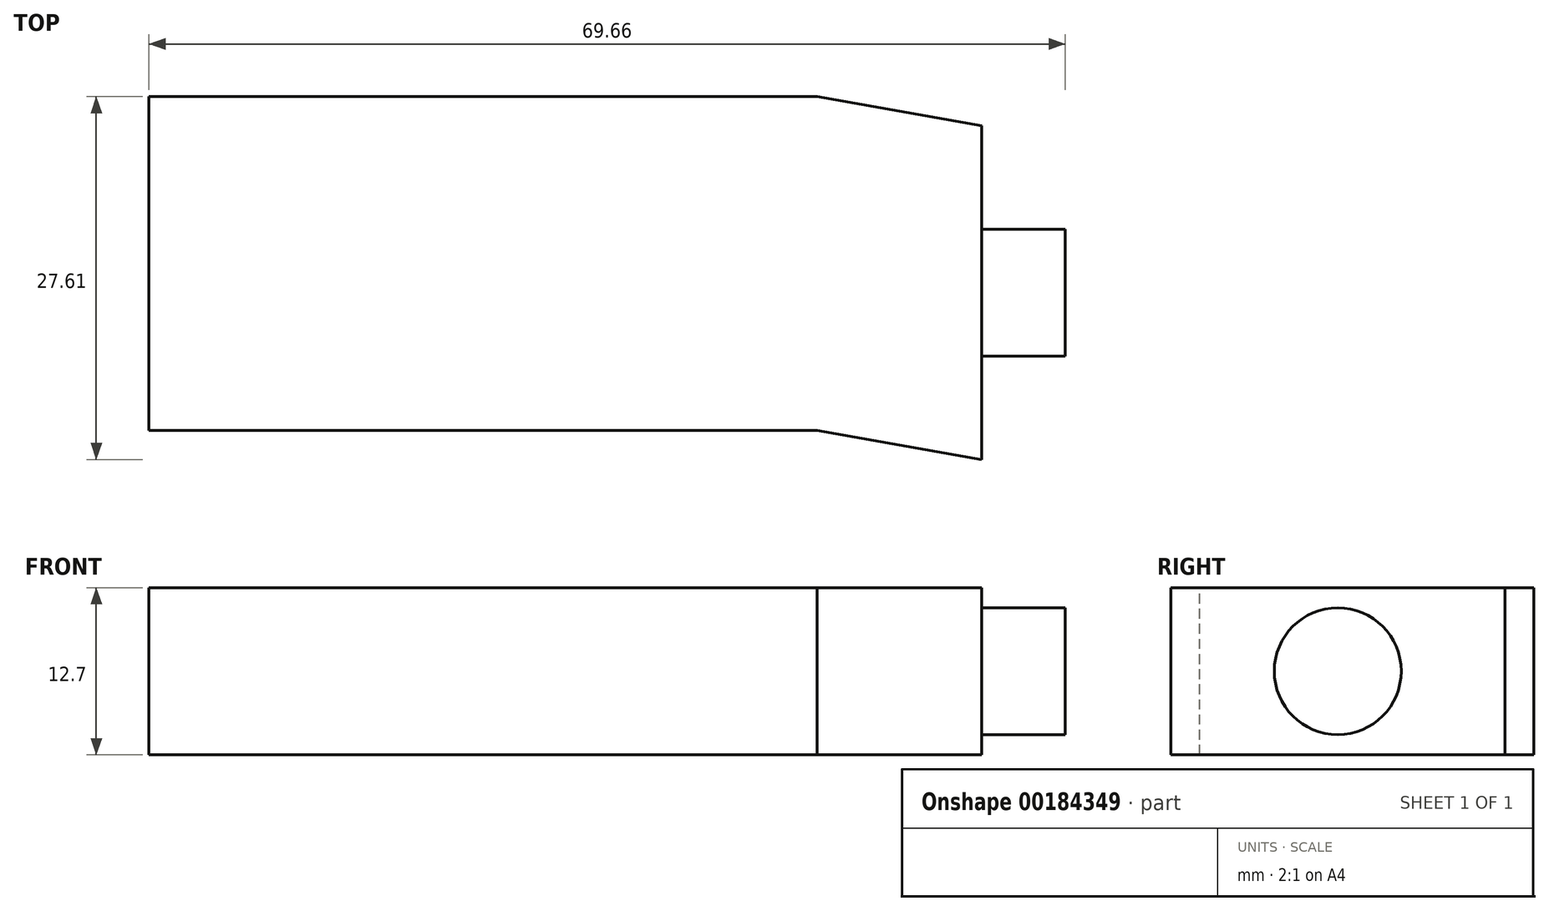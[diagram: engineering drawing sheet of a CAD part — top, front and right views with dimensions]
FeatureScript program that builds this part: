
annotation { "Feature Type Name" : "Feature", "Feature Type Description" : "" }
export const myFeature = defineFeature(function(context is Context, id is Id, definition is map)
    precondition{}
    {
        {
            var Q0;
            Q0=qCreatedBy(makeId("Top.planeOp"),FACE);
            var sketch = newSketch(context, id + "F0", { "sketchPlane" : qUnion([Q0])});
            skLineSegment(sketch, "E0.bottom", {"start": v(-25.4, 12.7) * mm, "end": v(25.4, 12.7) * mm});
            skLineSegment(sketch, "E0.top", {"start": v(-25.4, -12.7) * mm, "end": v(25.4, -12.7) * mm});
            skLineSegment(sketch, "E0.left", {"start": v(-25.4, 12.7) * mm, "end": v(-25.4, -12.7) * mm});
            skLineSegment(sketch, "E0.right", {"start": v(25.4, 12.7) * mm, "end": v(25.4, -12.7) * mm});
            skPoint(sketch, "E0.middle", {"position": v(0, 0) * mm});
            skLineSegment(sketch, "E1", {"start": v(25.4, -12.7) * mm, "end": v(37.9, -14.9) * mm});
            skLineSegment(sketch, "E2", {"start": v(25.4, 12.7) * mm, "end": v(37.9, 10.5) * mm});
            skLineSegment(sketch, "E3", {"start": v(37.9, 10.5) * mm, "end": v(37.9, -14.9) * mm});
            skLineSegment(sketch, "E4", {"start": v(37.9, 10.5) * mm, "end": v(37.9, -2.2) * mm});
            skSolve(sketch);
        }
        {
            var Q0;
            {var subQ1=sQuery(id+"F0.wireOp",EDGE,"E0.bottom");Q0=makeQuery(id+"F0.imprint","IMPRINT",FACE,{"disambiguationData":[TD([[makeQuery(id+"F0.imprint","IMPRINT",EDGE,{"derivedFrom":subQ1}),-1.0]])]});}
            var Q1;
            {var subQ0=sQuery(id+"F0.wireOp",EDGE,"E2");Q1=makeQuery(id+"F0.imprint","IMPRINT",FACE,{"disambiguationData":[TD([[makeQuery(id+"F0.imprint","IMPRINT",EDGE,{"derivedFrom":subQ0}),-1.0]])]});}
            var Q2;
            {var subQ0=sQuery(id+"F0.wireOp",EDGE,"E1");Q2=makeQuery(id+"F0.imprint","IMPRINT",FACE,{"disambiguationData":[TD([[makeQuery(id+"F0.imprint","IMPRINT",EDGE,{"derivedFrom":subQ0}),1.0]])]});}
            var Q3;
            {var subQ0=sQuery(id+"F0.wireOp",EDGE,"x6ou94J2-EOuo-O75U-wm8q-2U1nYv5dNW8F");Q3=makeQuery(id+"F0.imprint","IMPRINT",FACE,{"disambiguationData":[TD([[makeQuery(id+"F0.imprint","IMPRINT",EDGE,{"derivedFrom":subQ0}),-1.0]])]});}
            var Q4;
            {var subQ0=sQuery(id+"F0.wireOp",EDGE,"x6ou94J2-EOuo-O75U-wm8q-2U1nYv5dNW8F");Q4=makeQuery(id+"F0.imprint","IMPRINT",FACE,{"disambiguationData":[TD([[makeQuery(id+"F0.imprint","IMPRINT",EDGE,{"derivedFrom":subQ0}),1.0]])]});}
            extrude(context, id + "F1", {"entities" : qUnion([Q0, Q1, Q2, Q3, Q4]), "oppositeDirection" : true, "depth" : 12.7 * mm});
        }
        {
            var Q0;
            Q0=makeQuery(id+"F1.opExtrude","SWEPT_FACE",FACE,{"disambiguationData":[OSD([sQuery(id+"F0.wireOp",EDGE,"E3"),sQuery(id+"F0.wireOp",EDGE,"E4")])]});
            var sketch = newSketch(context, id + "F2", { "sketchPlane" : qUnion([Q0])});
            skLineSegment(sketch, "E5", {"start": v(10.5, 0) * mm, "end": v(10.5, -6.35) * mm});
            skLineSegment(sketch, "E6", {"start": v(10.5, -6.35) * mm, "end": v(-2.2, -6.35) * mm});
            skPoint(sketch, "E6.endSnap0", {"position": v(-2.2, 0) * mm});
            skCircle(sketch, "E7", {"center": v(-2.2, -6.35) * mm, "radius": 4.83 * mm});
            skSolve(sketch);
        }
        {
            var Q0;
            Q0=makeQuery(id+"F2.imprint","IMPRINT",FACE,{"disambiguationData":[TD([[makeQuery(id+"F2.imprint","IMPRINT",EDGE,{"derivedFrom":sQuery(id+"F2.wireOp",EDGE,"E7")}),1.0]])]});
            extrude(context, id + "F3", {"entities" : qUnion([Q0]), "operationType" : NewBodyOperationType.ADD, "depth" : 6.35 * mm});
        }
    });
